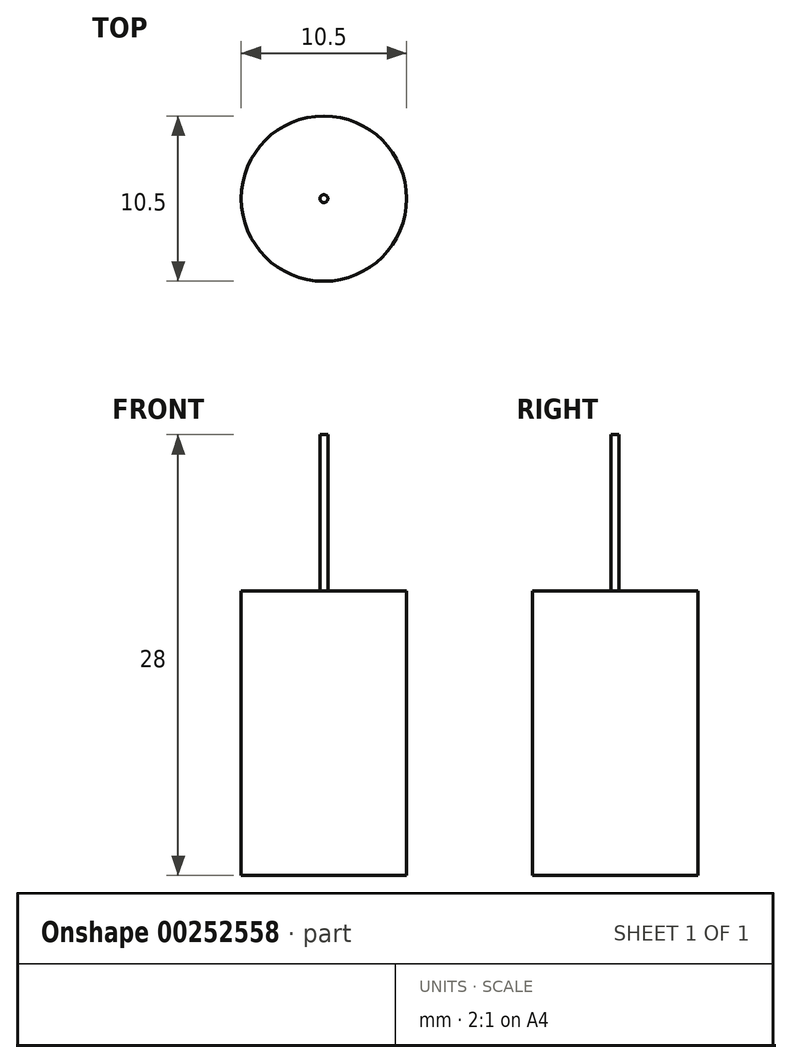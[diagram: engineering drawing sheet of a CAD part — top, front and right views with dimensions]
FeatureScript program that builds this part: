
annotation { "Feature Type Name" : "Feature", "Feature Type Description" : "" }
export const myFeature = defineFeature(function(context is Context, id is Id, definition is map)
    precondition{}
    {
        {
            var Q0;
            Q0=qCreatedBy(makeId("Front.planeOp"),FACE);
            var sketch = newSketch(context, id + "F0", { "sketchPlane" : qUnion([Q0])});
            skLineSegment(sketch, "E0.bottom", {"start": v(-5.25, -9.04) * mm, "end": v(5.25, -9.04) * mm});
            skLineSegment(sketch, "E0.top", {"start": v(-5.25, 9.04) * mm, "end": v(5.25, 9.04) * mm});
            skLineSegment(sketch, "E0.left", {"start": v(-5.25, -9.04) * mm, "end": v(-5.25, 9.04) * mm});
            skLineSegment(sketch, "E0.right", {"start": v(5.25, -9.04) * mm, "end": v(5.25, 9.04) * mm});
            skPoint(sketch, "E0.middle", {"position": v(0, 0) * mm});
            skLineSegment(sketch, "E1", {"start": v(0, 9.04) * mm, "end": v(0, -9.04) * mm});
            skSolve(sketch);
        }
        {
            var Q0;
            {var subQ0=sQuery(id+"F0.wireOp",EDGE,"E0.left");Q0=makeQuery(id+"F0.imprint","IMPRINT",FACE,{"disambiguationData":[TD([[makeQuery(id+"F0.imprint","IMPRINT",EDGE,{"derivedFrom":subQ0}),-1.0]])]});}
            var Q1;
            Q1=sQuery(id+"F0.wireOp",EDGE,"E1");
            revolve(context, id + "F1", {"entities" : qUnion([Q0]), "axis" : qUnion([Q1]), "revolveType" : RevolveType.FULL, "oppositeDirection" : true});
        }
        {
            var Q0;
            Q0=makeQuery(id+"F1.opRevolve","SWEPT_FACE",FACE,{"disambiguationData":[OSD([sQuery(id+"F0.wireOp",EDGE,"E0.top")])]});
            shell(context, id + "F2", {"entities" : qUnion([Q0]), "thickness" : 5 * mm});
        }
        {
            var Q0;
            Q0=makeQuery(id+"F2.opShell","OFFSET_FACE",FACE,{"disambiguationData":[OSD([sQuery(id+"F0.wireOp",EDGE,"E0.bottom")])]});
            extrude(context, id + "F3", {"entities" : qUnion([Q0]), "operationType" : NewBodyOperationType.ADD, "depth" : 23 * mm});
        }
    });
